# Revit family: Shower_Head-Grohe-Spa-Rainshower_F_Series_10-26872000
name_source: partatom
category: Plumbing Fixtures
units: mm (PartAtom-declared; Revit-internal decimal feet)

## family parameters
Always vertical = No
Cut with Voids When Loaded = No
OmniClass Number = 23.45.05.14.17
OmniClass Title = Showers
Part Type = Normal
Room Calculation Point = No
Round Connector Dimension = Use Diameter
Shared = Yes
Work Plane-Based = Yes

## types (1)
- 26872000
    27487 = No
    27489 = No
    ASME A112.18.1/CSA B125.1 = Yes
    Assembly Code = D2010710
    CW Connection = No
    CWFU = 3
    Default Elevation = 0"
    Description = Rainshower 10" Shower Head- 1 Spray
    Finish = Metal-Grohe-000-StarLight Chrome
    Flow Rate = 2.5gpm (9.5L/min)
    GROHE DreamSpray = Yes
    GROHE DripStop = Yes
    GROHE StarLight = Yes
    HW Connection = No
    HWFU = 3
    Height = 1 5/8"
    Manufacturer = Grohe
    Material = Metal-Grohe-000-StarLight Chrome
    Model = 26872000
    Price = Prices may vary. Please consult Manufacturer Representative for most up-to-date price list.
    Speed Clean = Yes
    Tempered Connection Diameter = 1/2"
    Tempered Connection Radius = 1/4"
    Tempered Water Connection = Yes
    URL = https://www.grohe.ca
    Vent Connection = No
    WFU = 4
    Waste Connection = No
    Width = 10"
    cUPC Compliant = Yes

## geometry (parser evidence)
native form markers: Sweep x2
no freeform markers — native parametric forms only
